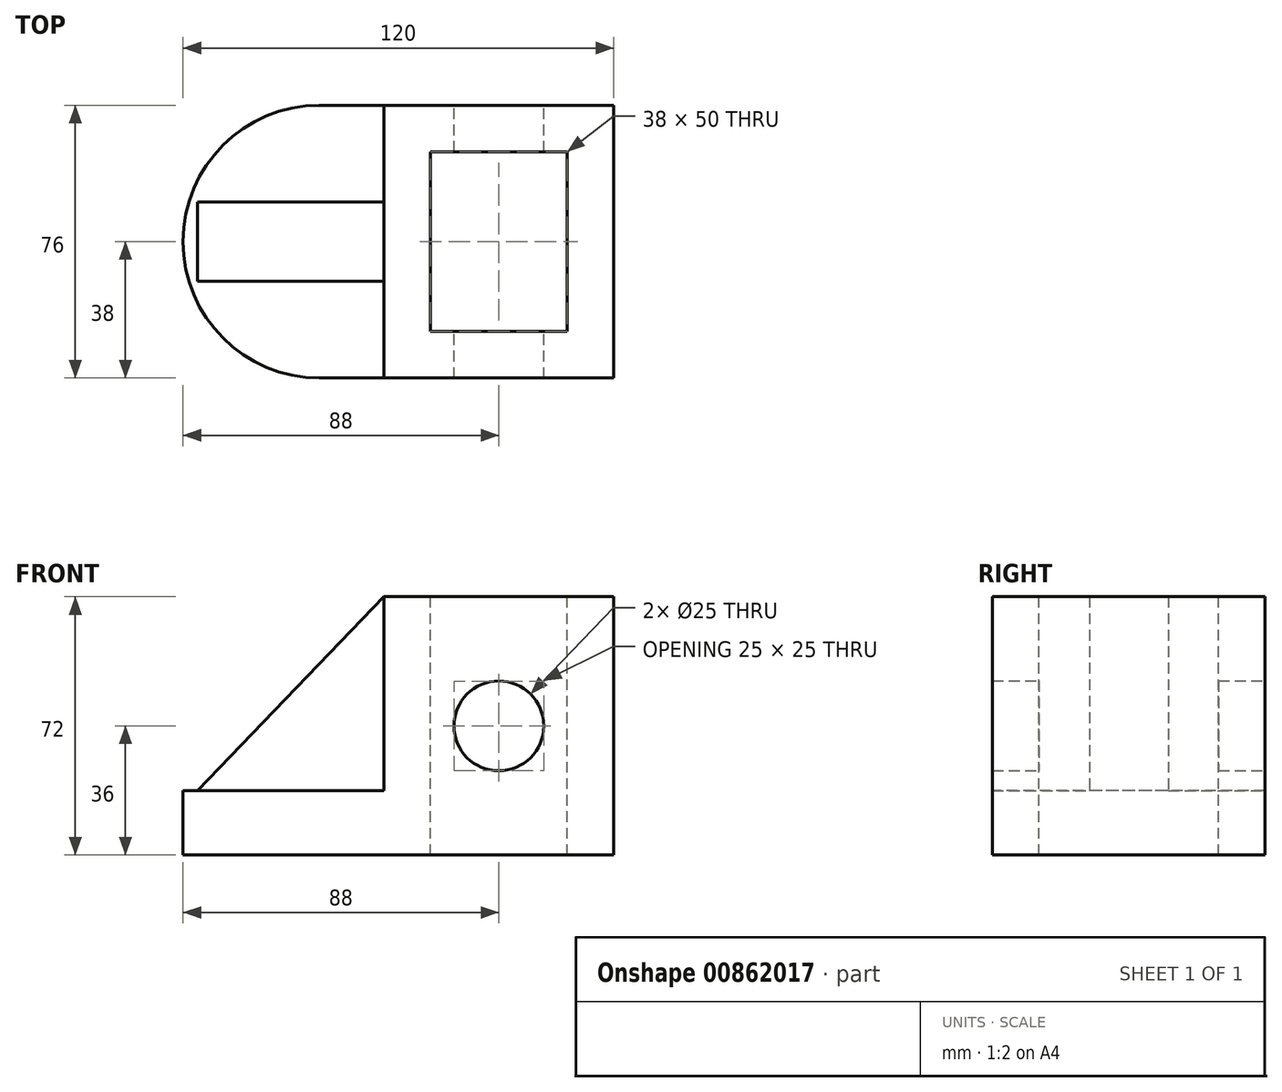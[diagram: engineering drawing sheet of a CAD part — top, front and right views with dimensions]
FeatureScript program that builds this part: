
annotation { "Feature Type Name" : "Feature", "Feature Type Description" : "" }
export const myFeature = defineFeature(function(context is Context, id is Id, definition is map)
    precondition{}
    {
        {
            var Q0;
            Q0=qCreatedBy(makeId("Front.planeOp"),FACE);
            var sketch = newSketch(context, id + "F0", { "sketchPlane" : qUnion([Q0])});
            skLineSegment(sketch, "E0", {"start": v(0, 0) * mm, "end": v(120, 0) * mm});
            skLineSegment(sketch, "E1", {"start": v(120, 0) * mm, "end": v(120, 72) * mm});
            skLineSegment(sketch, "E2", {"start": v(120, 72) * mm, "end": v(56, 72) * mm});
            skLineSegment(sketch, "E3", {"start": v(56, 72) * mm, "end": v(56, 18) * mm});
            skLineSegment(sketch, "E4", {"start": v(56, 18) * mm, "end": v(0, 18) * mm});
            skLineSegment(sketch, "E5", {"start": v(0, 18) * mm, "end": v(0, 0) * mm});
            skCircle(sketch, "E6", {"center": v(88, 36) * mm, "radius": 12.5 * mm});
            skPoint(sketch, "E6.centerSnap0", {"position": v(88, 72) * mm});
            skPoint(sketch, "E6.centerSnap1", {"position": v(120, 36) * mm});
            skSolve(sketch);
        }
        {
            var Q0;
            Q0=makeQuery(id+"F0.imprint","IMPRINT",FACE,{"disambiguationData":[TD([[makeQuery(id+"F0.imprint","IMPRINT",EDGE,{"derivedFrom":sQuery(id+"F0.wireOp",EDGE,"E0")}),1.0]])]});
            extrude(context, id + "F1", {"entities" : qUnion([Q0]), "depth" : 76 * mm, "offsetDistance" : 25 * mm});
        }
        {
            var Q0;
            Q0=makeQuery(id+"F1.opExtrude","SWEPT_FACE",FACE,{"disambiguationData":[OSD([sQuery(id+"F0.wireOp",EDGE,"E2")])]});
            var sketch = newSketch(context, id + "F2", { "sketchPlane" : qUnion([Q0])});
            skLineSegment(sketch, "E7.bottom", {"start": v(107, -13) * mm, "end": v(69, -13) * mm});
            skLineSegment(sketch, "E7.top", {"start": v(107, -63) * mm, "end": v(69, -63) * mm});
            skLineSegment(sketch, "E7.left", {"start": v(107, -13) * mm, "end": v(107, -63) * mm});
            skLineSegment(sketch, "E7.right", {"start": v(69, -13) * mm, "end": v(69, -63) * mm});
            skSolve(sketch);
        }
        {
            var Q0;
            Q0=makeQuery(id+"F2.imprint","IMPRINT",FACE,{"disambiguationData":[TD([[makeQuery(id+"F2.imprint","IMPRINT",EDGE,{"derivedFrom":sQuery(id+"F2.wireOp",EDGE,"E7.bottom")}),1.0]])]});
            extrude(context, id + "F3", {"entities" : qUnion([Q0]), "operationType" : NewBodyOperationType.REMOVE, "oppositeDirection" : true, "depth" : 116.9 * mm, "offsetDistance" : 25 * mm});
        }
        {
            var Q0;
            Q0=makeQuery(id+"F1.opExtrude","SWEPT_FACE",FACE,{"disambiguationData":[OSD([sQuery(id+"F0.wireOp",EDGE,"E4")])]});
            var sketch = newSketch(context, id + "F4", { "sketchPlane" : qUnion([Q0])});
            skArc(sketch, "E8", {"start": v(38, 0) * mm, "mid": v(0, -38) * mm, "end": v(38, -76) * mm});
            skPoint(sketch, "E9.start.orphan", {"position": v(0, -38) * mm});
            skSolve(sketch);
        }
        {
            var Q0;
            {var subQ0=sQuery(id+"F4.wireOp",EDGE,"E8");var subQ1=sQuery(id+"F0.wireOp",EDGE,"E4");var subQ2=makeQuery(id+"F1.opExtrude","CAP_EDGE",EDGE,{"disambiguationData":[OSD([subQ1])],"isStart":false});var subQ3=makeQuery(id+"F4.imprint","INTERSECT",VERTEX,{"derivedFrom":[subQ2,subQ0]});Q0=makeQuery(id+"F4.imprint","IMPRINT",FACE,{"disambiguationData":[TD([[makeQuery(id+"F4.imprint","IMPRINT",EDGE,{"disambiguationData":[TD([[subQ3,1.0]])],"derivedFrom":subQ0}),-1.0]])]});}
            var Q1;
            {var subQ0=sQuery(id+"F4.wireOp",EDGE,"E8");var subQ1=sQuery(id+"F0.wireOp",EDGE,"E4");var subQ2=makeQuery(id+"F1.opExtrude","CAP_EDGE",EDGE,{"disambiguationData":[OSD([subQ1])],"isStart":true});var subQ3=makeQuery(id+"F4.imprint","INTERSECT",VERTEX,{"derivedFrom":[subQ2,subQ0]});Q1=makeQuery(id+"F4.imprint","IMPRINT",FACE,{"disambiguationData":[TD([[makeQuery(id+"F4.imprint","IMPRINT",EDGE,{"disambiguationData":[TD([[subQ3,-1.0]])],"derivedFrom":subQ0}),-1.0]])]});}
            extrude(context, id + "F5", {"entities" : qUnion([Q0, Q1]), "operationType" : NewBodyOperationType.REMOVE, "oppositeDirection" : true, "depth" : 123.5 * mm, "offsetDistance" : 25 * mm});
        }
        {
            var Q0;
            Q0=makeQuery(id+"F1.opExtrude","SWEPT_FACE",FACE,{"disambiguationData":[OSD([sQuery(id+"F0.wireOp",EDGE,"E4")])]});
            var sketch = newSketch(context, id + "F6", { "sketchPlane" : qUnion([Q0])});
            skLineSegment(sketch, "E10", {"start": v(56, -38) * mm, "end": v(56, -27) * mm});
            skLineSegment(sketch, "E11", {"start": v(56, -27) * mm, "end": v(4, -27) * mm});
            skLineSegment(sketch, "E12", {"start": v(56, -38) * mm, "end": v(56, -49) * mm});
            skLineSegment(sketch, "E13", {"start": v(56, -49) * mm, "end": v(4, -49) * mm});
            skPoint(sketch, "E14.start.orphan", {"position": v(0, -38) * mm});
            skLineSegment(sketch, "E15", {"start": v(4, -27) * mm, "end": v(4, -49) * mm});
            skSolve(sketch);
        }
        {
            var Q0;
            Q0=makeQuery(id+"F6.imprint","IMPRINT",FACE,{"disambiguationData":[TD([[makeQuery(id+"F6.imprint","IMPRINT",EDGE,{"derivedFrom":sQuery(id+"F6.wireOp",EDGE,"E10")}),1.0]])]});
            extrude(context, id + "F7", {"entities" : qUnion([Q0]), "operationType" : NewBodyOperationType.ADD, "depth" : 54 * mm, "offsetDistance" : 25 * mm});
        }
        {
            var Q0;
            Q0=makeQuery(id+"F7.opExtrude","SWEPT_FACE",FACE,{"disambiguationData":[OSD([sQuery(id+"F6.wireOp",EDGE,"E13")])]});
            var sketch = newSketch(context, id + "F8", { "sketchPlane" : qUnion([Q0])});
            skLineSegment(sketch, "E16", {"start": v(4, 18) * mm, "end": v(56, 72) * mm});
            skLineSegment(sketch, "E17", {"start": v(56, 72) * mm, "end": v(4, 72) * mm});
            skLineSegment(sketch, "E18", {"start": v(4, 72) * mm, "end": v(4, 18) * mm});
            skSolve(sketch);
        }
        {
            var Q0;
            Q0=makeQuery(id+"F8.imprint","IMPRINT",FACE,{"disambiguationData":[TD([[makeQuery(id+"F8.imprint","IMPRINT",EDGE,{"derivedFrom":sQuery(id+"F8.wireOp",EDGE,"E16")}),1.0]])]});
            extrude(context, id + "F9", {"entities" : qUnion([Q0]), "operationType" : NewBodyOperationType.REMOVE, "oppositeDirection" : true, "depth" : 25 * mm, "offsetDistance" : 25 * mm});
        }
    });
